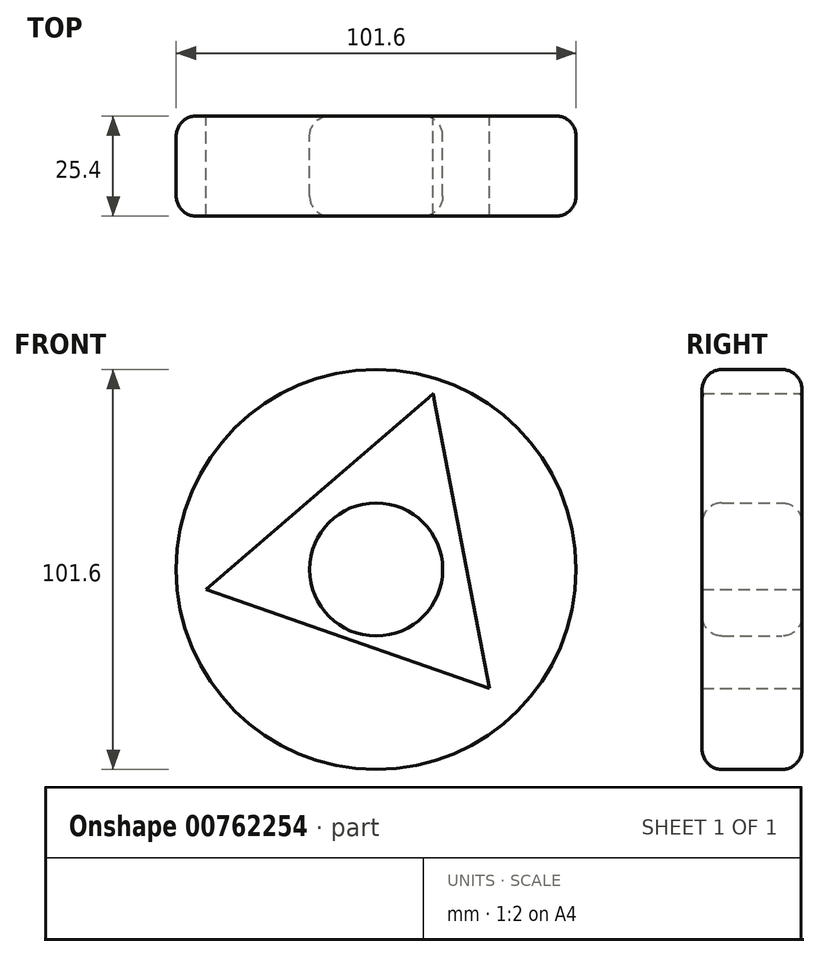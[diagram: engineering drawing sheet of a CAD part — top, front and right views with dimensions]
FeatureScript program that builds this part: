
annotation { "Feature Type Name" : "Feature", "Feature Type Description" : "" }
export const myFeature = defineFeature(function(context is Context, id is Id, definition is map)
    precondition{}
    {
        {
            var Q0;
            Q0=qCreatedBy(makeId("Front.planeOp"),FACE);
            var sketch = newSketch(context, id + "F0", { "sketchPlane" : qUnion([Q0])});
            skCircle(sketch, "E0", {"center": v(0, 0) * mm, "radius": 50.8 * mm});
            skCircle(sketch, "E1.cCircle", {"center": v(0, 3.14) * mm, "radius": 22 * mm, "construction": true});
            skLineSegment(sketch, "E1.0", {"start": v(-43.22, -5.09) * mm, "end": v(14.48, 44.68) * mm});
            skLineSegment(sketch, "E1.1", {"start": v(14.48, 44.68) * mm, "end": v(28.73, -30.17) * mm});
            skLineSegment(sketch, "E1.2", {"start": v(28.73, -30.17) * mm, "end": v(-43.22, -5.09) * mm});
            skPoint(sketch, "E1.0.midPoint", {"position": v(-14.37, 19.8) * mm});
            skSolve(sketch);
        }
        {
            var Q0;
            Q0 = qSketchRegion(id + "F0", true);
            extrude(context, id + "F1", {"entities" : qUnion([Q0]), "depth" : 25.4 * mm, "offsetDistance" : 25.4 * mm});
        }
        {
            var Q0;
            Q0=qCreatedBy(makeId("Front.planeOp"),FACE);
            var sketch = newSketch(context, id + "F2", { "sketchPlane" : qUnion([Q0])});
            skCircle(sketch, "E2", {"center": v(0, 0) * mm, "radius": 16.9 * mm});
            skLineSegment(sketch, "E3", {"start": v(14.3, 44.08) * mm, "end": v(-7.56, -17.8) * mm});
            skLineSegment(sketch, "E4", {"start": v(-26.63, 8.26) * mm, "end": v(25.07, -10.01) * mm});
            skSolve(sketch);
        }
        {
            var Q0;
            Q0 = qSketchRegion(id + "F2", true);
            extrude(context, id + "F3", {"entities" : qUnion([Q0]), "depth" : 25.4 * mm, "offsetDistance" : 25.4 * mm});
        }
        {
            var Q0;
            Q0=makeQuery(id+"F3.opExtrude","CAP_FACE",FACE,{"disambiguationData":[OSD([sQuery(id+"F2.wireOp",EDGE,"E2")])],"isStart":false});
            var Q1;
            Q1=makeQuery(id+"F3.opExtrude","CAP_FACE",FACE,{"disambiguationData":[OSD([sQuery(id+"F2.wireOp",EDGE,"E2")])],"isStart":true});
            var Q2;
            Q2=makeQuery(id+"F1.opExtrude","SWEPT_FACE",FACE,{"disambiguationData":[OSD([sQuery(id+"F0.wireOp",EDGE,"E0")])]});
            fillet(context, id + "F4", {"entities" : qUnion([Q0, Q1, Q2]), "radius" : 5.08 * mm, "tangentPropagation" : true, "allowEdgeOverflow" : false});
        }
    });
